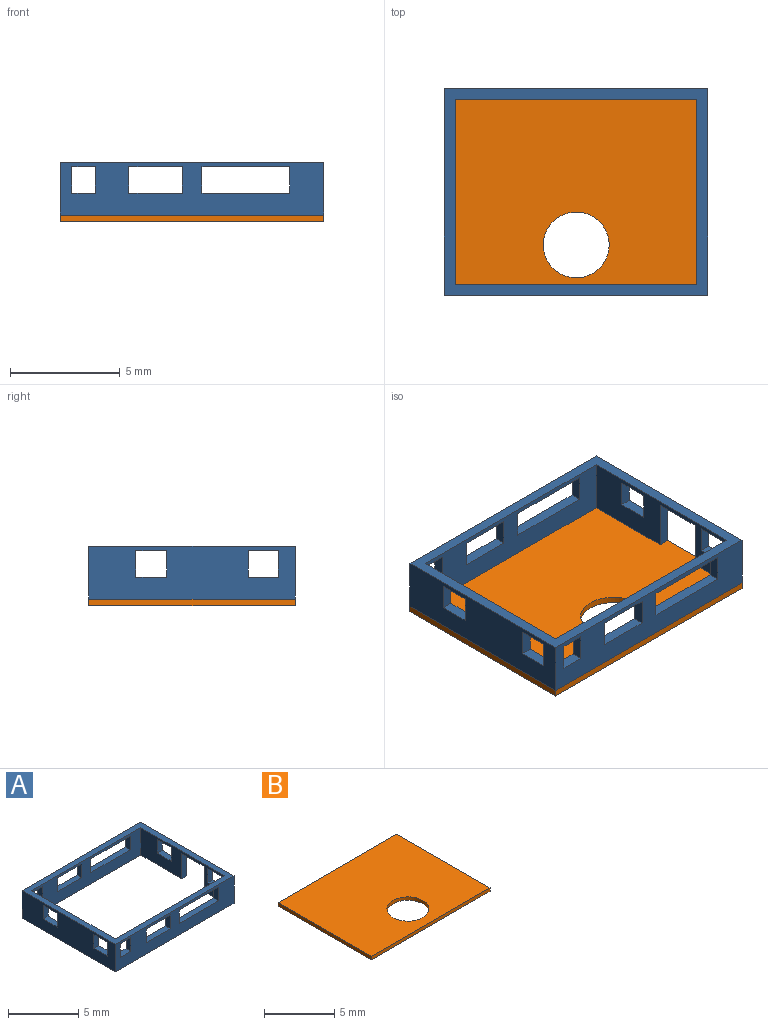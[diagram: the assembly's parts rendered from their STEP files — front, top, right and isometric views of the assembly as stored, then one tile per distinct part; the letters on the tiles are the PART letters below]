
ASSEMBLY  parts=2 mates=1
PART A: 53 faces, bbox 12x9.4x2.4 mm
  f0: plane 8.42x2.4mm, normal (-1,0,0), area 11.9mm2, adj f4,f7,f8,f9,f34,f35,f36,f37
  f1: plane 9.4x2.4mm, normal (1,0,0), area 14.3mm2, adj f5,f6,f8,f9,f34,f35,f36,f37
  f2: plane 8.42x2.4mm, normal (1,0,0), area 16.9mm2, adj f4,f7,f8,f9,f42,f43,f44,f45
  f3: plane 9.4x2.4mm, normal (-1,0,0), area 19.2mm2, adj f5,f6,f8,f9,f42,f43,f44,f45
  f4: plane 11.02x2.4mm, normal (0,1,0), area 17.4mm2, adj f0,f2,f8,f9,f22,f23,f24,f25
  f5: plane 12x2.4mm, normal (0,-1,0), area 19.8mm2, adj f1,f3,f8,f9,f22,f23,f24,f25
  f6: plane 12x2.4mm, normal (0,1,0), area 19.8mm2, adj f1,f3,f8,f9,f10,f11,f12,f13
  f7: plane 11.02x2.4mm, normal (0,-1,0), area 17.4mm2, adj f0,f2,f8,f9,f10,f11,f12,f13
  f8: plane 12x9.4mm, normal (0,0,1), area 20mm2, adj f0,f1,f2,f3,f4,f5,f6,f7
  f9: plane 12x9.4mm, normal (0,0,-1), area 18.9mm2, adj f0,f1,f2,f3,f4,f5,f6,f7
  f10: plane 1.2x0.49mm, normal (-1,0,0), area 0.6mm2, adj f6,f7,f11,f13
  f11: plane 3.99x0.49mm, normal (0,0,1), area 2mm2, adj f6,f7,f10,f12
  f12: plane 1.2x0.49mm, normal (1,0,0), area 0.6mm2, adj f6,f7,f11,f13
  f13: plane 3.99x0.49mm, normal (0,0,-1), area 2mm2, adj f6,f7,f10,f12
  f14: plane 2.43x0.49mm, normal (0,0,1), area 1.2mm2, adj f6,f7,f15,f17
  f15: plane 1.2x0.49mm, normal (1,0,0), area 0.6mm2, adj f6,f7,f14,f16
  f16: plane 2.43x0.49mm, normal (0,0,-1), area 1.2mm2, adj f6,f7,f15,f17
  f17: plane 1.2x0.49mm, normal (-1,0,0), area 0.6mm2, adj f6,f7,f14,f16
  f18: plane 1.2x0.49mm, normal (-1,0,0), area 0.6mm2, adj f6,f7,f19,f21
  f19: plane 1.08x0.49mm, normal (0,0,1), area 0.5mm2, adj f6,f7,f18,f20
  f20: plane 1.2x0.49mm, normal (1,0,0), area 0.6mm2, adj f6,f7,f19,f21
  f21: plane 1.08x0.49mm, normal (0,0,-1), area 0.5mm2, adj f6,f7,f18,f20
  f22: plane 3.99x0.49mm, normal (0,0,-1), area 2mm2, adj f4,f5,f23,f25
  f23: plane 1.2x0.49mm, normal (1,0,0), area 0.6mm2, adj f4,f5,f22,f24
  f24: plane 3.99x0.49mm, normal (0,0,1), area 2mm2, adj f4,f5,f23,f25
  f25: plane 1.2x0.49mm, normal (-1,0,0), area 0.6mm2, adj f4,f5,f22,f24
  f26: plane 1.2x0.49mm, normal (-1,0,0), area 0.6mm2, adj f4,f5,f27,f29
  f27: plane 2.43x0.49mm, normal (0,0,-1), area 1.2mm2, adj f4,f5,f26,f28
  f28: plane 1.2x0.49mm, normal (1,0,0), area 0.6mm2, adj f4,f5,f27,f29
  f29: plane 2.43x0.49mm, normal (0,0,1), area 1.2mm2, adj f4,f5,f26,f28
  f30: plane 1.08x0.49mm, normal (0,0,-1), area 0.5mm2, adj f4,f5,f31,f33
  f31: plane 1.2x0.49mm, normal (1,0,0), area 0.6mm2, adj f4,f5,f30,f32
  f32: plane 1.08x0.49mm, normal (0,0,1), area 0.5mm2, adj f4,f5,f31,f33
  f33: plane 1.2x0.49mm, normal (-1,0,0), area 0.6mm2, adj f4,f5,f30,f32
  f34: plane 1.2x0.49mm, normal (0,-1,0), area 0.6mm2, adj f0,f1,f35,f37
  f35: plane 1.37x0.49mm, normal (0,0,1), area 0.7mm2, adj f0,f1,f34,f36
  f36: plane 1.2x0.49mm, normal (0,1,0), area 0.6mm2, adj f0,f1,f35,f37
  f37: plane 1.37x0.49mm, normal (0,0,-1), area 0.7mm2, adj f0,f1,f34,f36
  f38: plane 1.2x0.49mm, normal (0,-1,0), area 0.6mm2, adj f0,f1,f39,f41
  f39: plane 1.41x0.49mm, normal (0,0,1), area 0.7mm2, adj f0,f1,f38,f40
  f40: plane 1.2x0.49mm, normal (0,1,0), area 0.6mm2, adj f0,f1,f39,f41
  f41: plane 1.41x0.49mm, normal (0,0,-1), area 0.7mm2, adj f0,f1,f38,f40
  f42: plane 1.37x0.49mm, normal (0,0,-1), area 0.7mm2, adj f2,f3,f43,f45
  f43: plane 1.2x0.49mm, normal (0,1,0), area 0.6mm2, adj f2,f3,f42,f44
  f44: plane 1.37x0.49mm, normal (0,0,1), area 0.7mm2, adj f2,f3,f43,f45
  f45: plane 1.2x0.49mm, normal (0,-1,0), area 0.6mm2, adj f2,f3,f42,f44
  f46: plane 1.41x0.49mm, normal (0,0,-1), area 0.7mm2, adj f2,f3,f47,f49
  f47: plane 1.2x0.49mm, normal (0,1,0), area 0.6mm2, adj f2,f3,f46,f48
  f48: plane 1.41x0.49mm, normal (0,0,1), area 0.7mm2, adj f2,f3,f47,f49
  f49: plane 1.2x0.49mm, normal (0,-1,0), area 0.6mm2, adj f2,f3,f46,f48
  f50: plane 2.25x0.49mm, normal (0,0,-1), area 1.1mm2, adj f0,f1,f51,f52
  f51: plane 2.2x0.49mm, normal (0,1,0), area 1.1mm2, adj f0,f1,f9,f50
  f52: plane 2.2x0.49mm, normal (0,-1,0), area 1.1mm2, adj f0,f1,f9,f50
PART B: 7 faces, bbox 12x9.4x0.3 mm
  f0: plane 9.4x0.3mm, normal (-1,0,0), area 2.8mm2, adj f1,f3,f4,f5
  f1: plane 12x0.3mm, normal (0,-1,0), area 3.6mm2, adj f0,f2,f4,f5
  f2: plane 9.4x0.3mm, normal (1,0,0), area 2.8mm2, adj f1,f3,f4,f5
  f3: plane 12x0.3mm, normal (0,1,0), area 3.6mm2, adj f0,f2,f4,f5
  f4: plane 12x9.4mm, normal (0,0,-1), area 105.7mm2, adj f0,f1,f2,f3,f6
  f5: plane 12x9.4mm, normal (0,0,1), area 105.7mm2, adj f0,f1,f2,f3,f6
  f6: cylinder r=1.5mm len=3mm, axis (0,0,1), area 2.8mm2, adj f4,f5
PLACE A t=(-3.52,-0.16,2.88)mm
PLACE B t=(-3.52,-0.16,2.88)mm
MATE planar A.f9 <-> B.f5  axis (0,0,-1) through (8.48,-0.16,2.88)mm
